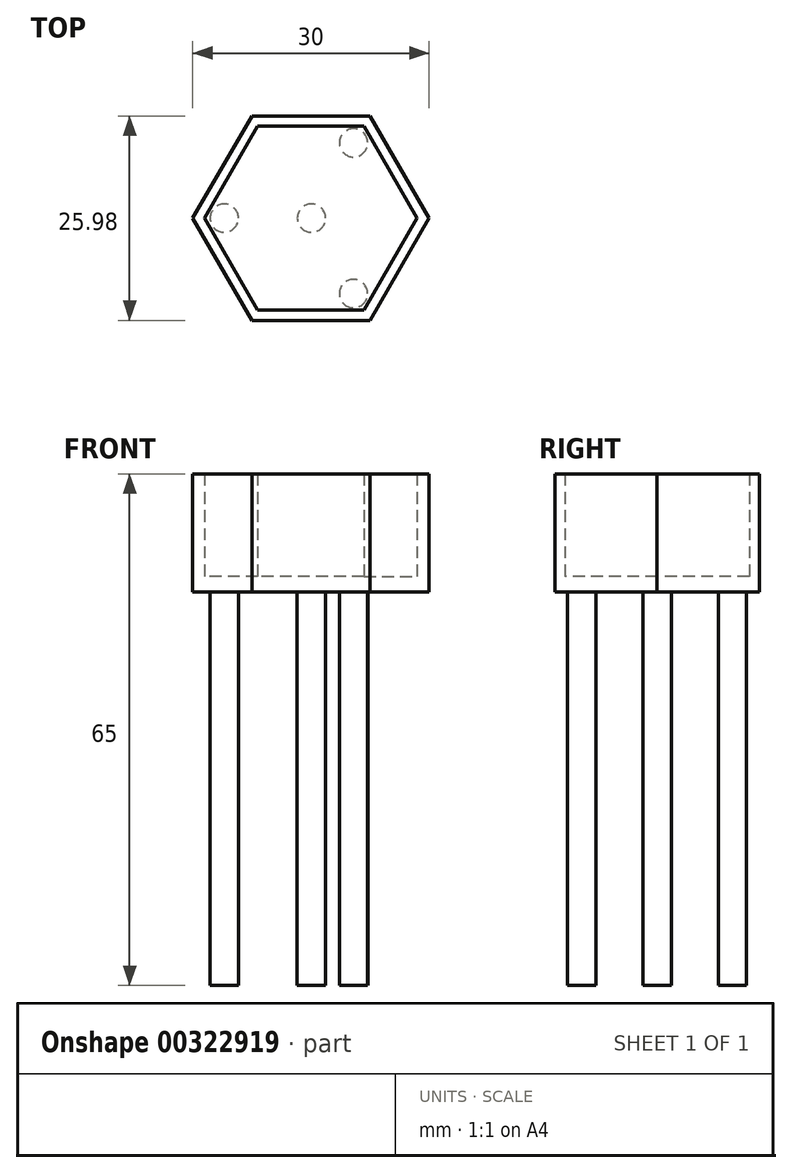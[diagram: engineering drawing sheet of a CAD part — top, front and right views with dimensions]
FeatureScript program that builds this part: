
annotation { "Feature Type Name" : "Feature", "Feature Type Description" : "" }
export const myFeature = defineFeature(function(context is Context, id is Id, definition is map)
    precondition{}
    {
        {
            var Q0;
            Q0=qCreatedBy(makeId("Top.planeOp"),FACE);
            var sketch = newSketch(context, id + "F0", { "sketchPlane" : qUnion([Q0])});
            skCircle(sketch, "E0.cCircle", {"center": v(0, 0) * mm, "radius": 15 * mm, "construction": true});
            skLineSegment(sketch, "E0.0", {"start": v(15, 0) * mm, "end": v(7.5, -13) * mm});
            skLineSegment(sketch, "E0.1", {"start": v(7.5, -13) * mm, "end": v(-7.5, -13) * mm});
            skLineSegment(sketch, "E0.2", {"start": v(-7.5, -13) * mm, "end": v(-15, 0) * mm});
            skLineSegment(sketch, "E0.3", {"start": v(-15, 0) * mm, "end": v(-7.5, 13) * mm});
            skLineSegment(sketch, "E0.4", {"start": v(-7.5, 13) * mm, "end": v(7.5, 13) * mm});
            skLineSegment(sketch, "E0.5", {"start": v(7.5, 13) * mm, "end": v(15, 0) * mm});
            skCircle(sketch, "E1.cCircle", {"center": v(0, 0) * mm, "radius": 13.5 * mm, "construction": true});
            skLineSegment(sketch, "E1.0", {"start": v(13.5, 0) * mm, "end": v(6.75, -11.7) * mm});
            skLineSegment(sketch, "E1.1", {"start": v(6.75, -11.7) * mm, "end": v(-6.75, -11.7) * mm});
            skLineSegment(sketch, "E1.2", {"start": v(-6.75, -11.7) * mm, "end": v(-13.5, 0) * mm});
            skLineSegment(sketch, "E1.3", {"start": v(-13.5, 0) * mm, "end": v(-6.75, 11.7) * mm});
            skLineSegment(sketch, "E1.4", {"start": v(-6.75, 11.7) * mm, "end": v(6.75, 11.7) * mm});
            skLineSegment(sketch, "E1.5", {"start": v(6.75, 11.7) * mm, "end": v(13.5, 0) * mm});
            skSolve(sketch);
        }
        {
            var Q0;
            Q0=makeQuery(id+"F0.imprint","IMPRINT",FACE,{"disambiguationData":[TD([[makeQuery(id+"F0.imprint","IMPRINT",EDGE,{"derivedFrom":sQuery(id+"F0.wireOp",EDGE,"E0.0")}),-1.0]])]});
            extrude(context, id + "F1", {"entities" : qUnion([Q0]), "depth" : 15 * mm});
        }
        {
            var Q0;
            Q0=makeQuery(id+"F0.imprint","IMPRINT",FACE,{"disambiguationData":[TD([[makeQuery(id+"F0.imprint","IMPRINT",EDGE,{"derivedFrom":sQuery(id+"F0.wireOp",EDGE,"E1.0")}),-1.0]])]});
            extrude(context, id + "F2", {"entities" : qUnion([Q0]), "operationType" : NewBodyOperationType.ADD, "depth" : 2 * mm});
        }
        {
            var Q0;
            Q0=qCreatedBy(makeId("Top.planeOp"),FACE);
            var sketch = newSketch(context, id + "F3", { "sketchPlane" : qUnion([Q0])});
            skCircle(sketch, "E2", {"center": v(-11, 0) * mm, "radius": 1.8 * mm});
            skCircle(sketch, "E3", {"center": v(5.43, 9.57) * mm, "radius": 1.8 * mm});
            skCircle(sketch, "E4", {"center": v(5.4, -9.58) * mm, "radius": 1.8 * mm});
            skCircle(sketch, "E5", {"center": v(0.07, 0) * mm, "radius": 1.8 * mm});
            skSolve(sketch);
        }
        {
            var Q0;
            Q0=makeQuery(id+"F3.imprint","IMPRINT",FACE,{"disambiguationData":[TD([[makeQuery(id+"F3.imprint","IMPRINT",EDGE,{"derivedFrom":sQuery(id+"F3.wireOp",EDGE,"E2")}),1.0]])]});
            var Q1;
            Q1=makeQuery(id+"F3.imprint","IMPRINT",FACE,{"disambiguationData":[TD([[makeQuery(id+"F3.imprint","IMPRINT",EDGE,{"derivedFrom":sQuery(id+"F3.wireOp",EDGE,"E3")}),1.0]])]});
            var Q2;
            Q2=makeQuery(id+"F3.imprint","IMPRINT",FACE,{"disambiguationData":[TD([[makeQuery(id+"F3.imprint","IMPRINT",EDGE,{"derivedFrom":sQuery(id+"F3.wireOp",EDGE,"E4")}),1.0]])]});
            var Q3;
            Q3=makeQuery(id+"F3.imprint","IMPRINT",FACE,{"disambiguationData":[TD([[makeQuery(id+"F3.imprint","IMPRINT",EDGE,{"derivedFrom":sQuery(id+"F3.wireOp",EDGE,"E5")}),1.0]])]});
            extrude(context, id + "F4", {"entities" : qUnion([Q0, Q1, Q2, Q3]), "operationType" : NewBodyOperationType.ADD, "oppositeDirection" : true, "depth" : 50 * mm});
        }
    });
